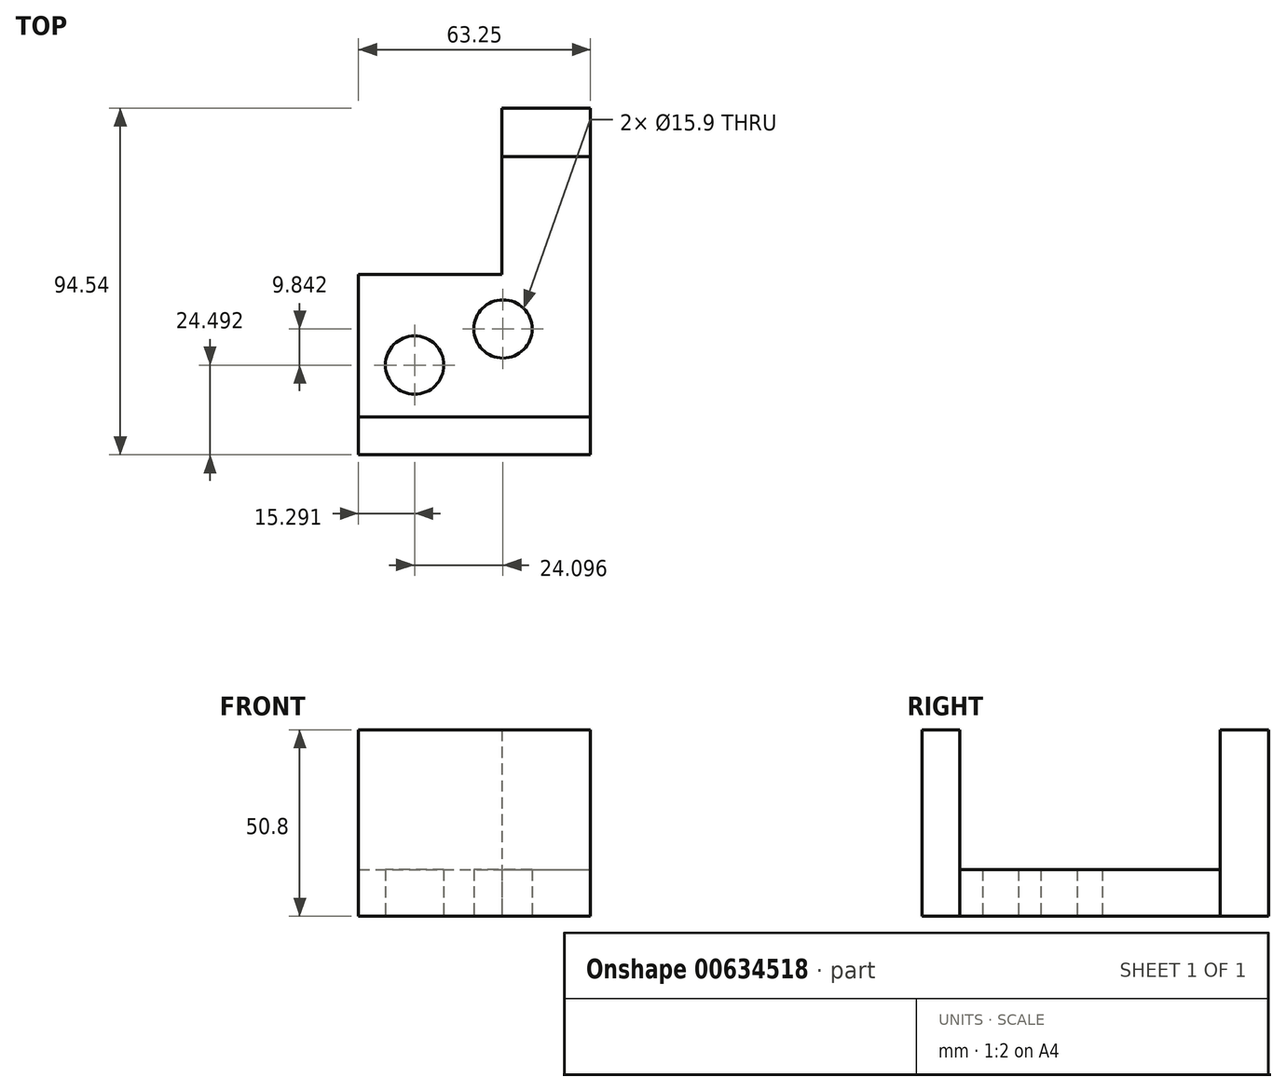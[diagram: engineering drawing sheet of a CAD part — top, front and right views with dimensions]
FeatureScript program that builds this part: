
annotation { "Feature Type Name" : "Feature", "Feature Type Description" : "" }
export const myFeature = defineFeature(function(context is Context, id is Id, definition is map)
    precondition{}
    {
        {
            var Q0;
            Q0=qCreatedBy(makeId("Top.planeOp"),FACE);
            var sketch = newSketch(context, id + "F0", { "sketchPlane" : qUnion([Q0])});
            skLineSegment(sketch, "E0", {"start": v(-21.57, 17.2) * mm, "end": v(17.54, 17.2) * mm});
            skLineSegment(sketch, "E1", {"start": v(17.54, 17.2) * mm, "end": v(17.54, 62.58) * mm});
            skLineSegment(sketch, "E2", {"start": v(17.54, 62.58) * mm, "end": v(41.68, 62.58) * mm});
            skLineSegment(sketch, "E3", {"start": v(41.68, 62.58) * mm, "end": v(41.68, -31.96) * mm});
            skLineSegment(sketch, "E4", {"start": v(41.68, -31.96) * mm, "end": v(-21.57, -31.96) * mm});
            skLineSegment(sketch, "E5", {"start": v(-21.57, 17.2) * mm, "end": v(-21.57, -31.96) * mm});
            skPoint(sketch, "E6.orphan", {"position": v(-23.13, -31.96) * mm});
            skLineSegment(sketch, "E7", {"start": v(-21.57, -21.63) * mm, "end": v(41.68, -21.63) * mm});
            skLineSegment(sketch, "E8", {"start": v(17.54, 49.34) * mm, "end": v(41.68, 49.34) * mm});
            skCircle(sketch, "E9", {"center": v(-6.28, -7.47) * mm, "radius": 7.95 * mm});
            skCircle(sketch, "E10", {"center": v(17.82, 2.37) * mm, "radius": 7.95 * mm});
            skSolve(sketch);
        }
        {
            var Q0;
            {var subQ0=sQuery(id+"F0.wireOp",EDGE,"E2");Q0=makeQuery(id+"F0.imprint","IMPRINT",FACE,{"disambiguationData":[TD([[makeQuery(id+"F0.imprint","IMPRINT",EDGE,{"derivedFrom":subQ0}),-1.0]])]});}
            var Q1;
            {var subQ0=sQuery(id+"F0.wireOp",EDGE,"E4");Q1=makeQuery(id+"F0.imprint","IMPRINT",FACE,{"disambiguationData":[TD([[makeQuery(id+"F0.imprint","IMPRINT",EDGE,{"derivedFrom":subQ0}),-1.0]])]});}
            extrude(context, id + "F1", {"entities" : qUnion([Q0, Q1]), "depth" : 50.8 * mm, "offsetDistance" : 25.4 * mm});
        }
        {
            var Q0;
            {var subQ1=sQuery(id+"F0.wireOp",EDGE,"E0");Q0=makeQuery(id+"F0.imprint","IMPRINT",FACE,{"disambiguationData":[TD([[makeQuery(id+"F0.imprint","IMPRINT",EDGE,{"derivedFrom":subQ1}),-1.0]])]});}
            extrude(context, id + "F2", {"entities" : qUnion([Q0]), "depth" : 12.7 * mm, "offsetDistance" : 25.4 * mm});
        }
    });
